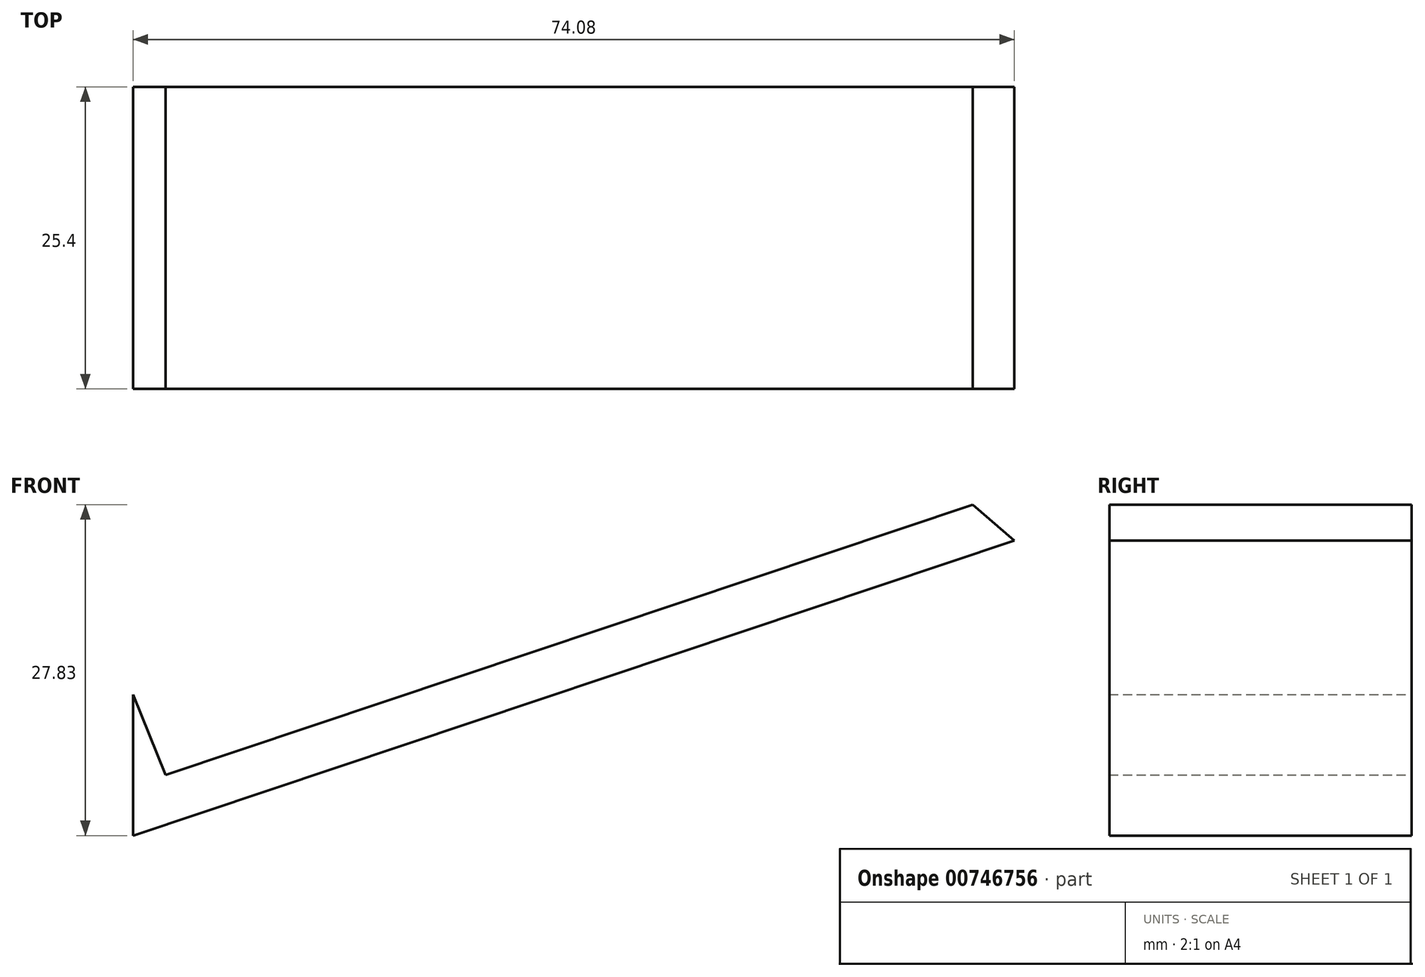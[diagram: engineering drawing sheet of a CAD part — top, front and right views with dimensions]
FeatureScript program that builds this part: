
annotation { "Feature Type Name" : "Feature", "Feature Type Description" : "" }
export const myFeature = defineFeature(function(context is Context, id is Id, definition is map)
    precondition{}
    {
        {
            var Q0;
            Q0=qCreatedBy(makeId("Front.planeOp"),FACE);
            var sketch = newSketch(context, id + "F0", { "sketchPlane" : qUnion([Q0])});
            skLineSegment(sketch, "E0", {"start": v(-53.37, 33.76) * mm, "end": v(-53.37, 21.9) * mm});
            skLineSegment(sketch, "E1", {"start": v(-53.37, 21.9) * mm, "end": v(20.7, 46.71) * mm});
            skLineSegment(sketch, "E2", {"start": v(-53.37, 33.76) * mm, "end": v(-50.63, 27) * mm});
            skLineSegment(sketch, "E3", {"start": v(-50.63, 27) * mm, "end": v(17.2, 49.73) * mm});
            skLineSegment(sketch, "E4", {"start": v(17.2, 49.73) * mm, "end": v(20.7, 46.71) * mm});
            skSolve(sketch);
        }
        {
            var Q0;
            Q0 = qSketchRegion(id + "F0", true);
            extrude(context, id + "F1", {"entities" : qUnion([Q0]), "depth" : 25.4 * mm, "offsetDistance" : 25.4 * mm});
        }
    });
